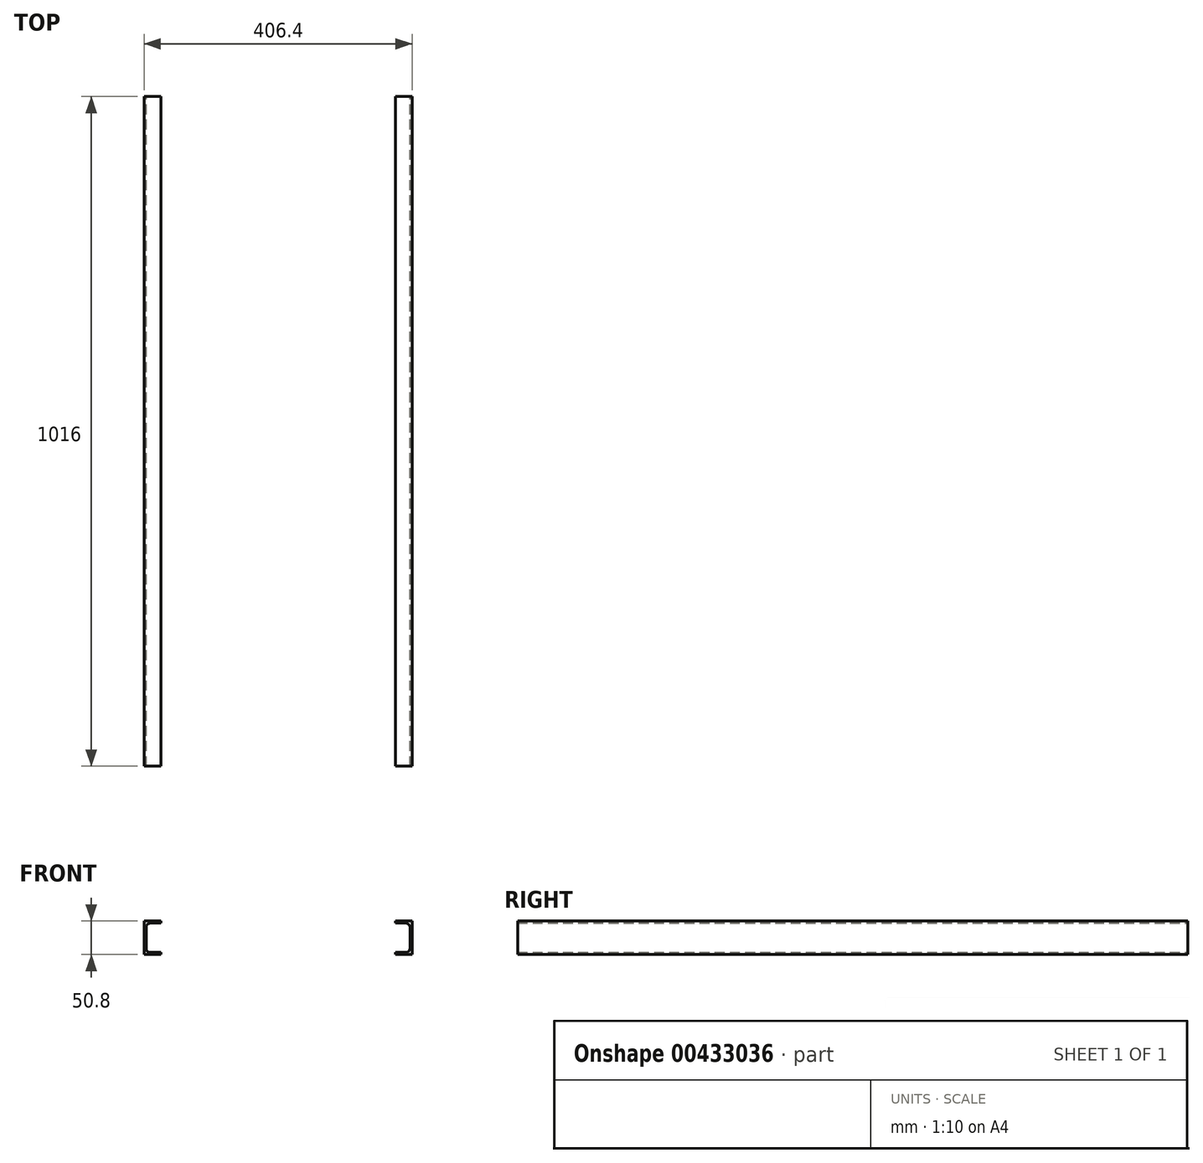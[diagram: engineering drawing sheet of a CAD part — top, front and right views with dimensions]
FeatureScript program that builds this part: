
annotation { "Feature Type Name" : "Feature", "Feature Type Description" : "" }
export const myFeature = defineFeature(function(context is Context, id is Id, definition is map)
    precondition{}
    {
        {
            var Q0;
            Q0=qCreatedBy(makeId("Front.planeOp"),FACE);
            var sketch = newSketch(context, id + "F0", { "sketchPlane" : qUnion([Q0])});
            skLineSegment(sketch, "E0", {"start": v(0, 0) * mm, "end": v(0, 50.8) * mm});
            skLineSegment(sketch, "E1", {"start": v(0, 50.8) * mm, "end": v(25.4, 50.8) * mm});
            skLineSegment(sketch, "E2", {"start": v(25.4, 50.8) * mm, "end": v(25.4, 47.63) * mm});
            skLineSegment(sketch, "E3", {"start": v(25.4, 47.63) * mm, "end": v(9.52, 47.63) * mm});
            skLineSegment(sketch, "E4", {"start": v(3.17, 41.28) * mm, "end": v(3.18, 9.52) * mm});
            skLineSegment(sketch, "E5", {"start": v(9.53, 3.17) * mm, "end": v(25.4, 3.18) * mm});
            skLineSegment(sketch, "E6", {"start": v(25.4, 3.18) * mm, "end": v(25.4, 0) * mm});
            skLineSegment(sketch, "E7", {"start": v(25.4, 0) * mm, "end": v(0, 0) * mm});
            skPoint(sketch, "E8.visualSharp", {"position": v(3.17, 47.62) * mm});
            skArc(sketch, "E8.filletArc", {"start": v(9.52, 47.63) * mm, "mid": v(5.03, 45.77) * mm, "end": v(3.17, 41.28) * mm});
            skPoint(sketch, "E9.visualSharp", {"position": v(3.18, 3.17) * mm});
            skArc(sketch, "E9.filletArc", {"start": v(3.18, 9.52) * mm, "mid": v(5.03, 5.03) * mm, "end": v(9.53, 3.17) * mm});
            skLineSegment(sketch, "E10", {"start": v(406.4, 0) * mm, "end": v(381, 0) * mm});
            skLineSegment(sketch, "E11", {"start": v(381, 0) * mm, "end": v(381, 3.17) * mm});
            skLineSegment(sketch, "E12", {"start": v(381, 3.17) * mm, "end": v(396.88, 3.17) * mm});
            skLineSegment(sketch, "E13", {"start": v(403.23, 9.52) * mm, "end": v(403.23, 41.27) * mm});
            skLineSegment(sketch, "E14", {"start": v(396.88, 47.62) * mm, "end": v(381, 47.62) * mm});
            skLineSegment(sketch, "E15", {"start": v(381, 47.62) * mm, "end": v(381, 50.8) * mm});
            skLineSegment(sketch, "E16", {"start": v(381, 50.8) * mm, "end": v(406.4, 50.8) * mm});
            skLineSegment(sketch, "E17", {"start": v(406.4, 50.8) * mm, "end": v(406.4, 0) * mm});
            skPoint(sketch, "E18.visualSharp", {"position": v(403.23, 47.62) * mm});
            skArc(sketch, "E18.filletArc", {"start": v(403.23, 41.27) * mm, "mid": v(401.37, 45.77) * mm, "end": v(396.88, 47.62) * mm});
            skPoint(sketch, "E19.visualSharp", {"position": v(403.23, 3.17) * mm});
            skArc(sketch, "E19.filletArc", {"start": v(396.88, 3.17) * mm, "mid": v(401.37, 5.03) * mm, "end": v(403.23, 9.52) * mm});
            skSolve(sketch);
        }
        {
            var Q0;
            Q0=makeQuery(id+"F0.imprint","IMPRINT",FACE,{"disambiguationData":[TD([[makeQuery(id+"F0.imprint","IMPRINT",EDGE,{"derivedFrom":sQuery(id+"F0.wireOp",EDGE,"E0")}),-1.0]])]});
            var Q1;
            Q1=makeQuery(id+"F0.imprint","IMPRINT",FACE,{"disambiguationData":[TD([[makeQuery(id+"F0.imprint","IMPRINT",EDGE,{"derivedFrom":sQuery(id+"F0.wireOp",EDGE,"E10")}),-1.0]])]});
            extrude(context, id + "F1", {"entities" : qUnion([Q0, Q1]), "depth" : 1016 * mm, "offsetDistance" : 25.4 * mm});
        }
    });
